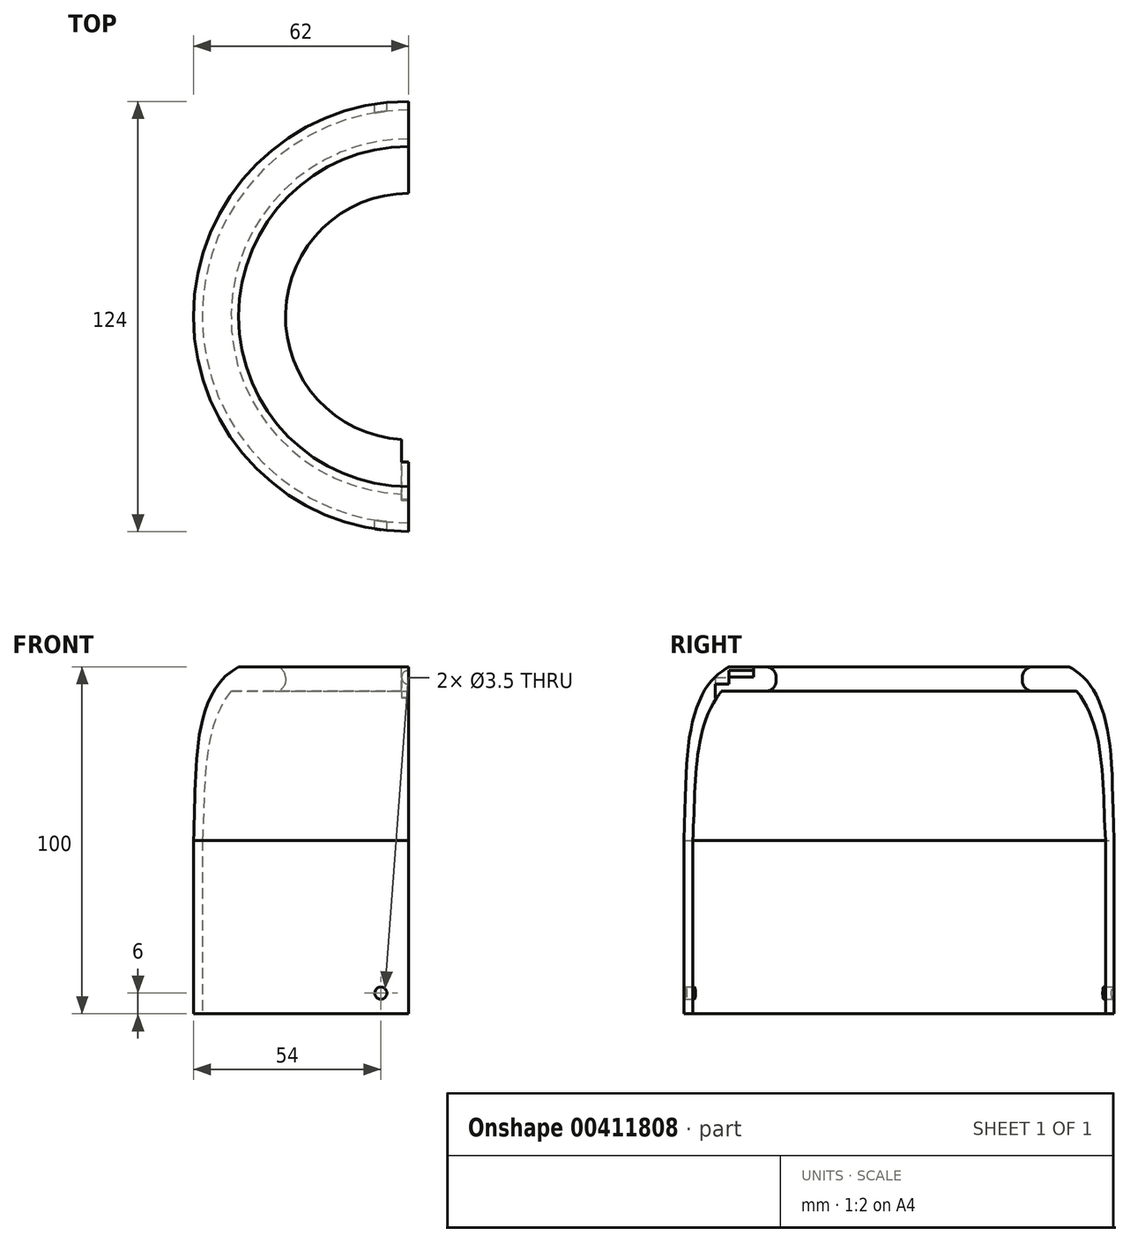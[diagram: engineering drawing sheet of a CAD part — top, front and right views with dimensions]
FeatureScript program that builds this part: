
annotation { "Feature Type Name" : "Feature", "Feature Type Description" : "" }
export const myFeature = defineFeature(function(context is Context, id is Id, definition is map)
    precondition{}
    {
        {
            var Q0;
            Q0=qCreatedBy(makeId("Front.planeOp"),FACE);
            var sketch = newSketch(context, id + "F0", { "sketchPlane" : qUnion([Q0])});
            skLineSegment(sketch, "E0", {"start": v(-38.5, 50) * mm, "end": v(-49, 50) * mm});
            skLineSegment(sketch, "E1", {"start": v(-62, 0) * mm, "end": v(-62, -50) * mm});
            skLineSegment(sketch, "E2", {"start": v(-35.5, 47) * mm, "end": v(-35.5, 46) * mm});
            skLineSegment(sketch, "E3", {"start": v(-38.5, 43) * mm, "end": v(-51.2, 43) * mm});
            skFitSpline(sketch, "E4", {"points": [v(-49, 50) * mm, v(-52.64, 47.47) * mm, v(-56.76, 41.98) * mm, v(-60.39, 29.9) * mm, v(-62, 0) * mm], "startDerivative": vector(-21.37, -10.6) * mm, "endDerivative": vector(-3.86, -109.3) * mm});
            skPoint(sketch, "E5.visualSharp", {"position": v(-35.5, 50) * mm});
            skArc(sketch, "E5.filletArc", {"start": v(-35.5, 47) * mm, "mid": v(-36.38, 49.12) * mm, "end": v(-38.5, 50) * mm});
            skPoint(sketch, "E6.visualSharp", {"position": v(-35.5, 43) * mm});
            skArc(sketch, "E6.filletArc", {"start": v(-38.5, 43) * mm, "mid": v(-36.38, 43.88) * mm, "end": v(-35.5, 46) * mm});
            skLineSegment(sketch, "E7", {"start": v(-62, -50) * mm, "end": v(0, -50) * mm});
            skLineSegment(sketch, "E8", {"start": v(-59.5, -50) * mm, "end": v(-59.5, 0) * mm});
            skFitSpline(sketch, "E9", {"points": [v(-51.2, 43) * mm, v(-59.5, 0) * mm], "startDerivative": vector(-25.81, -31.95) * mm, "endDerivative": vector(-3.04, -46.67) * mm});
            skLineSegment(sketch, "E10", {"start": v(0, -50) * mm, "end": v(0, -45.2) * mm});
            skSolve(sketch);
        }
        {
            var Q0;
            Q0=makeQuery(id+"F0.imprint","IMPRINT",FACE,{"disambiguationData":[TD([[makeQuery(id+"F0.imprint","IMPRINT",EDGE,{"derivedFrom":sQuery(id+"F0.wireOp",EDGE,"E0")}),1.0]])]});
            var Q1;
            Q1=sQuery(id+"F0.wireOp",EDGE,"E10");
            revolve(context, id + "F1", {"entities" : qUnion([Q0]), "axis" : qUnion([Q1]), "revolveType" : RevolveType.SYMMETRIC, "angle" : 180 * degree});
        }
        {
            var Q0;
            Q0=qCreatedBy(makeId("Front.planeOp"),FACE);
            var sketch = newSketch(context, id + "F2", { "sketchPlane" : qUnion([Q0])});
            skCircle(sketch, "E11", {"center": v(0, 47) * mm, "radius": 2 * mm});
            skLineSegment(sketch, "E12", {"start": v(-2, 47.07) * mm, "end": v(-2, 41.07) * mm});
            skLineSegment(sketch, "E13", {"start": v(-2, 41.07) * mm, "end": v(0, 41.07) * mm});
            skLineSegment(sketch, "E14", {"start": v(0, 41.07) * mm, "end": v(0, 45) * mm});
            skLineSegment(sketch, "E15", {"start": v(-2, 47.07) * mm, "end": v(-2, 50.36) * mm});
            skLineSegment(sketch, "E16", {"start": v(0, 50.36) * mm, "end": v(0, 49) * mm});
            skLineSegment(sketch, "E17", {"start": v(-2, 50.36) * mm, "end": v(0, 50.36) * mm});
            skSolve(sketch);
        }
        {
            var Q0;
            {var subQ1=sQuery(id+"F2.wireOp",EDGE,"E11");var subQ4=makeQuery(id+"F2.imprint","INTERSECT",VERTEX,{"derivedFrom":[subQ1,sQuery(id+"F2.wireOp",EDGE,"E14")]});Q0=makeQuery(id+"F2.imprint","IMPRINT",FACE,{"disambiguationData":[TD([[makeQuery(id+"F2.imprint","IMPRINT",EDGE,{"disambiguationData":[TD([[subQ4,1.0]])],"derivedFrom":subQ1}),1.0]])]});}
            extrude(context, id + "F3", {"entities" : qUnion([Q0]), "operationType" : NewBodyOperationType.REMOVE, "depth" : 49 * mm, "offsetDistance" : 25 * mm});
        }
        {
            var Q0;
            {var subQ0=sQuery(id+"F2.wireOp",EDGE,"E15");Q0=makeQuery(id+"F2.imprint","IMPRINT",FACE,{"disambiguationData":[TD([[makeQuery(id+"F2.imprint","IMPRINT",EDGE,{"derivedFrom":subQ0}),-1.0]])]});}
            extrude(context, id + "F4", {"entities" : qUnion([Q0]), "operationType" : NewBodyOperationType.REMOVE, "depth" : 42 * mm, "offsetDistance" : 25 * mm});
        }
        {
            var Q0;
            {var subQ4=sQuery(id+"F2.wireOp",EDGE,"E13");Q0=makeQuery(id+"F2.imprint","IMPRINT",FACE,{"disambiguationData":[TD([[makeQuery(id+"F2.imprint","IMPRINT",EDGE,{"derivedFrom":subQ4}),1.0]])]});}
            extrude(context, id + "F5", {"entities" : qUnion([Q0]), "operationType" : NewBodyOperationType.REMOVE, "depth" : 53 * mm, "offsetDistance" : 25 * mm});
        }
        {
            var Q0;
            Q0=qCreatedBy(makeId("Front.planeOp"),FACE);
            var sketch = newSketch(context, id + "F6", { "sketchPlane" : qUnion([Q0])});
            skCircle(sketch, "E18", {"center": v(-8, -44) * mm, "radius": 1.75 * mm});
            skSolve(sketch);
        }
        {
            var Q0;
            Q0=makeQuery(id+"F6.imprint","IMPRINT",FACE,{"disambiguationData":[TD([[makeQuery(id+"F6.imprint","IMPRINT",EDGE,{"derivedFrom":sQuery(id+"F6.wireOp",EDGE,"E18")}),1.0]])]});
            var Q1;
            Q1=sQuery(id+"F6.wireOp",EDGE,"E18");
            extrude(context, id + "F7", {"entities" : qUnion([Q0]), "operationType" : NewBodyOperationType.REMOVE, "surfaceEntities" : qUnion([Q1]), "depth" : 125 * mm, "symmetric" : true});
        }
    });
